# Revit family: Sink-Kitchen-KOHLER-Cape_Dory-K-5863
name_source: partatom
category: Plumbing Fixtures
revit_build: Autodesk Revit 2015 (Build: 20140606_1530(x64)
units: mm (PartAtom-declared; Revit-internal decimal feet)

## types (4) — shared parameters
ADA Compliant = No
Assembly Code = D2010400
CW Connection = No
Cold Water Inlet = Cold Water Inlet
Date Modified = 04/19/2019
Default Elevation = 36"
Description = 33 inch x 22 inch x 9-5/8 inch top-mount single-bowl kitchen sink with 4 faucet holes
Drain Included = No
HW Connection = No
Height = 9 5/8"
Hot Water Inlet = Hot Water Inlet
Length = 33"
Manufacturer = KOHLER Co.
MasterFormat 1995 = 15410
MasterFormat 2004 = 22.41.16
Material = Enameled Cast Iron
Product Documentation Link = https://www.us.kohler.com
Product Name = Cape Dory
Product Page URL = http://www.us.kohler.com
URL = https://www.us.kohler.com
Vent Connection = No
Waste Connection = Yes
Waste Water Outlet = Waste Water Outlet
WaterSense Certified = No
Width = 22"

## per-type parameters (varying)
| type | Finish | Model | Type |
| 0- White | Kohler-Enameled_Cast_Iron-0-White | K-5863-4-0 | 1 |
| 96- Biscuit | Kohler-Enameled_Cast_Iron-96-Biscuit | K-5863-4-96 | 2 |
| 47-Almond | Kohler-Enameled_Cast_Iron-47-Almond | K-5863-4-47 | 3 |
| 7- Black Black | Kohler-Enameled_Cast_Iron-7-Black_Black | K-5863-4-7 | 4 |

## geometry (parser evidence)
native form markers: Sweep x5
no freeform markers — native parametric forms only
